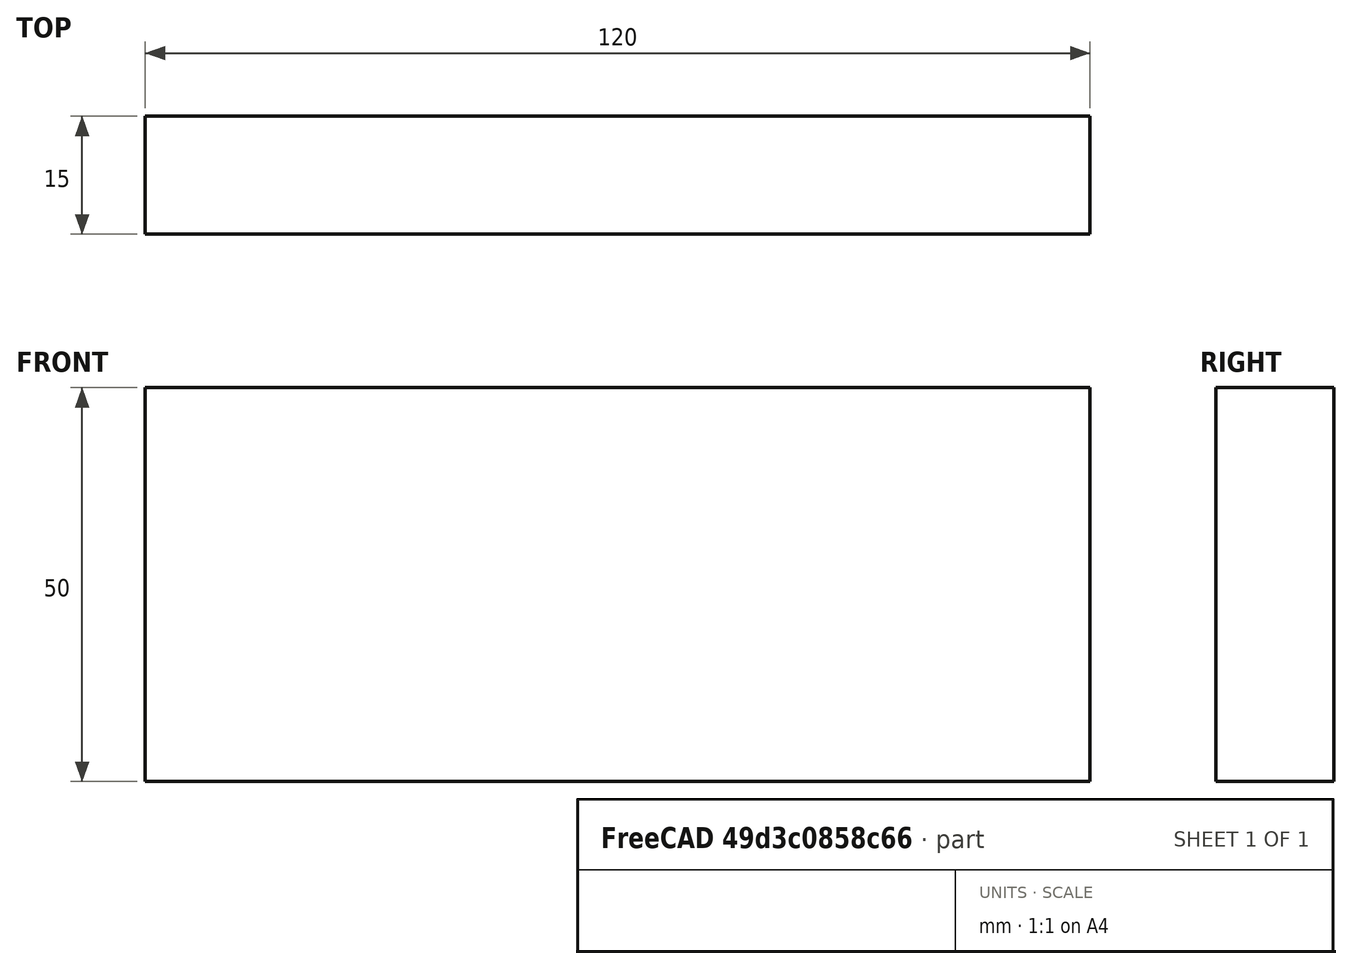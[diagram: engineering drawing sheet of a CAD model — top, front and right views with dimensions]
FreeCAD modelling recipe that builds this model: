
FCSTD DOCUMENT  (FreeCAD 0.15R4671 (Git))
Label: Flat Bar 120x15 EN10058 S235JR
License: All rights reserved
LicenseURL: http://en.wikipedia.org/wiki/All_rights_reserved
objects: Sketcher::SketchObject×1, Part::Extrusion×1
note: 2 computed .brp shape members not serialized (recipe doc carries the construction recipe); baked Part::Feature solids carry a one-line shape summary decoded from their .brp

FEATURE [Sketcher::SketchObject] Sketch
  sketch-geometry (4):
    g0: LineSegment StartX=-60 StartY=-7.5 StartZ=0 EndX=60 EndY=-7.5 EndZ=0
    g1: LineSegment StartX=60 StartY=-7.5 StartZ=0 EndX=60 EndY=7.5 EndZ=0
    g2: LineSegment StartX=60 StartY=7.5 StartZ=0 EndX=-60 EndY=7.5 EndZ=0
    g3: LineSegment StartX=-60 StartY=7.5 StartZ=0 EndX=-60 EndY=-7.5 EndZ=0
  constraints (12):
    c: Coincident(g0,g1)
    c: Coincident(g1,g2)
    c: Coincident(g2,g3)
    c: Coincident(g3,g0)
    c: Horizontal(g0)
    c: Horizontal(g2)
    c: Vertical(g1)
    c: Vertical(g3)
    c: Symmetric(g1,g2,g-2)
    c: Symmetric(g0,g1,g-1)
    c: DistanceY(g1) = 15
    c: DistanceX(g0) = 120
FEATURE [Part::Extrusion] Extrude  label="Flat Bar 120x15 EN10058 S235JR"
  Base = -> Sketch
  Dir = (0,0,50)
  Solid = true
